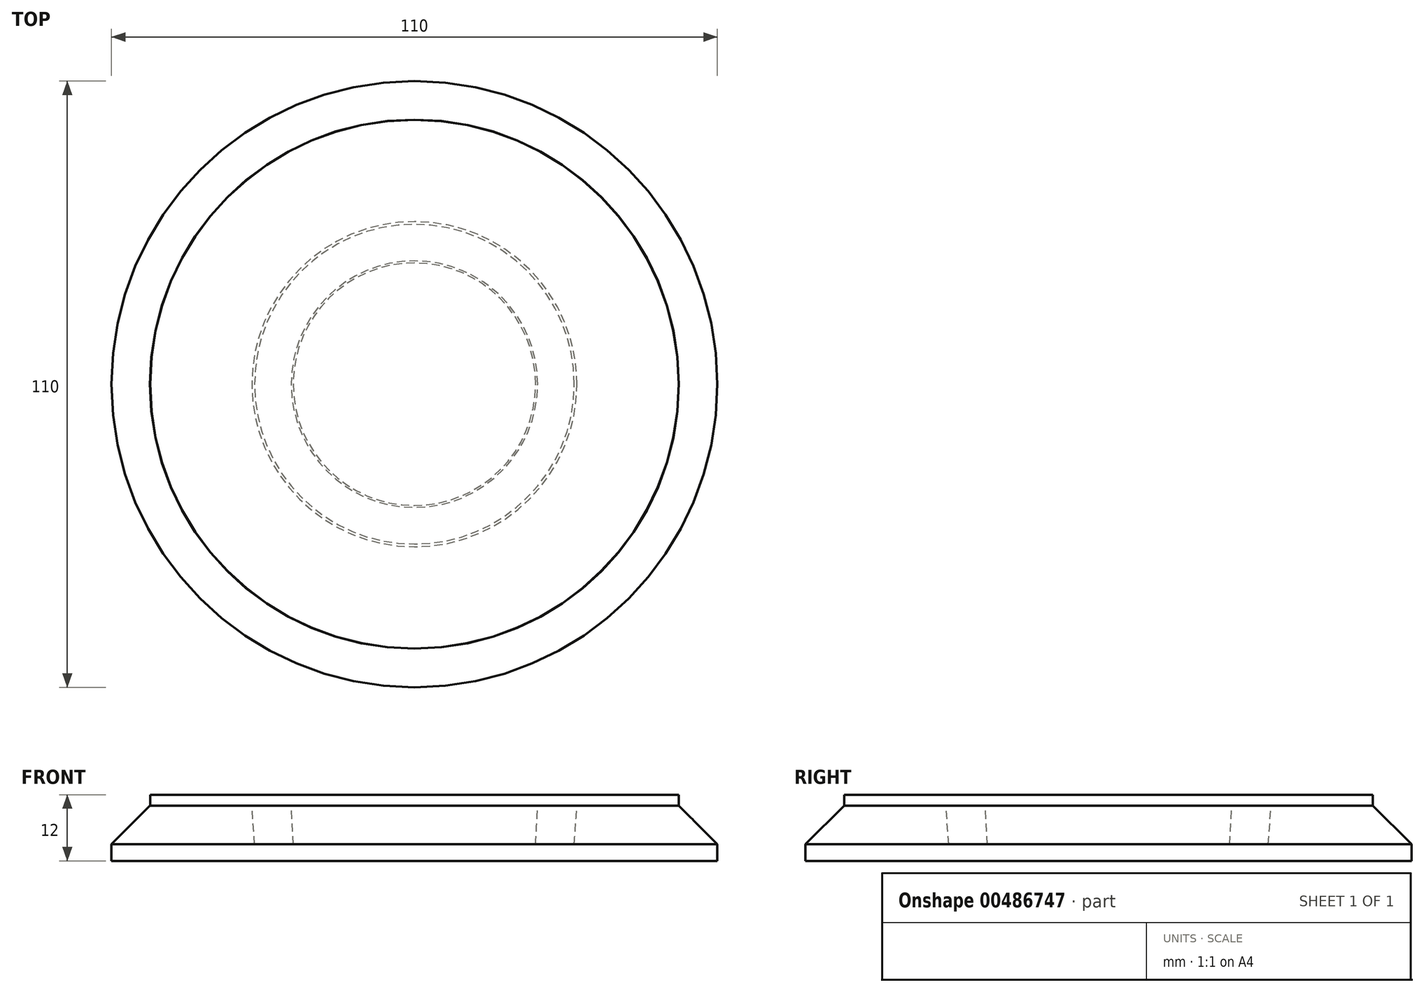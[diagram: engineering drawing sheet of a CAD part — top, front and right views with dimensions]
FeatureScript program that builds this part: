
annotation { "Feature Type Name" : "Feature", "Feature Type Description" : "" }
export const myFeature = defineFeature(function(context is Context, id is Id, definition is map)
    precondition{}
    {
        {
            var Q0;
            Q0=qCreatedBy(makeId("Top.planeOp"),FACE);
            var sketch = newSketch(context, id + "F0", { "sketchPlane" : qUnion([Q0])});
            skCircle(sketch, "E0", {"center": v(0, 0) * mm, "radius": 55 * mm});
            skSolve(sketch);
        }
        {
            var Q0;
            Q0=makeQuery(id+"F0.imprint","IMPRINT",FACE,{"disambiguationData":[TD([[makeQuery(id+"F0.imprint","IMPRINT",EDGE,{"derivedFrom":sQuery(id+"F0.wireOp",EDGE,"E0")}),1.0]])]});
            extrude(context, id + "F1", {"entities" : qUnion([Q0]), "depth" : 10 * mm});
        }
        {
            var Q0;
            Q0=makeQuery(id+"F1.opExtrude","CAP_EDGE",EDGE,{"disambiguationData":[OSD([sQuery(id+"F0.wireOp",EDGE,"E0")])],"isStart":false});
            chamfer(context, id + "F2", {"entities" : qUnion([Q0]), "width" : 7 * mm, "tangentPropagation" : true});
        }
        {
            var Q0;
            Q0=makeQuery(id+"F1.opExtrude","CAP_FACE",FACE,{"disambiguationData":[OSD([sQuery(id+"F0.wireOp",EDGE,"E0")])],"isStart":false});
            var sketch = newSketch(context, id + "F3", { "sketchPlane" : qUnion([Q0])});
            skCircle(sketch, "E1", {"center": v(0, 0) * mm, "radius": 29.5 * mm});
            skSolve(sketch);
        }
        {
            var Q0;
            Q0=makeQuery(id+"F3.imprint","IMPRINT",FACE,{"disambiguationData":[TD([[makeQuery(id+"F3.imprint","IMPRINT",EDGE,{"derivedFrom":sQuery(id+"F3.wireOp",EDGE,"E1")}),1.0]])]});
            extrude(context, id + "F4", {"entities" : qUnion([Q0]), "operationType" : NewBodyOperationType.REMOVE, "oppositeDirection" : true, "depth" : 7 * mm, "hasDraft" : true, "draftAngle" : 4 * degree, "draftPullDirection" : true});
        }
        {
            var Q0;
            Q0=makeQuery(id+"F4.boolean.opBoolean","COPY",FACE,{"derivedFrom":makeQuery(id+"F4.opExtrude","CAP_FACE",FACE,{"disambiguationData":[OSD([sQuery(id+"F3.wireOp",EDGE,"E1")])],"isStart":false})});
            var sketch = newSketch(context, id + "F5", { "sketchPlane" : qUnion([Q0])});
            skCircle(sketch, "E2", {"center": v(0, 0) * mm, "radius": 22 * mm});
            skSolve(sketch);
        }
        {
            var Q0;
            Q0 = qSketchRegion(id + "F5", true);
            var Q1;
            Q1=makeQuery(id+"F1.opExtrude","CAP_FACE",FACE,{"disambiguationData":[OSD([sQuery(id+"F0.wireOp",EDGE,"E0")])],"isStart":false});
            extrude(context, id + "F6", {"entities" : qUnion([Q0]), "endBound" : BoundingType.UP_TO_SURFACE, "endBoundEntityFace" : qUnion([Q1]), "depth" : 25 * mm, "hasDraft" : true, "draftAngle" : 3 * degree});
        }
        {
            var Q0;
            Q0=makeQuery(id+"F6.opExtrude","CAP_FACE",FACE,{"disambiguationData":[OSD([sQuery(id+"F5.wireOp",EDGE,"E2")])],"isStart":false});
            cPlane(context, id + "F7", {"entities" : qUnion([Q0]), "cplaneType" : CPlaneType.OFFSET, "offset" : 0 * mm, "width" : 150 * mm, "height" : 150 * mm});
        }
        {
            var Q0;
            Q0=qCreatedBy(id+"F7.planeOp",FACE);
            var sketch = newSketch(context, id + "F8", { "sketchPlane" : qUnion([Q0])});
            skCircle(sketch, "E3", {"center": v(0, 0) * mm, "radius": 47.96 * mm});
            skSolve(sketch);
        }
        {
            var Q0;
            Q0=makeQuery(id+"F8.imprint","IMPRINT",FACE,{"disambiguationData":[TD([[makeQuery(id+"F8.imprint","IMPRINT",EDGE,{"derivedFrom":sQuery(id+"F8.wireOp",EDGE,"E3")}),1.0]])]});
            extrude(context, id + "F9", {"entities" : qUnion([Q0]), "operationType" : NewBodyOperationType.ADD, "depth" : 2 * mm});
        }
    });
